# Revit family: HERZ Strömax 4125 AWD
name_source: partatom
category: Rohrzubehör
units: mm (PartAtom-declared; Revit-internal decimal feet)

## family parameters
Arbeitsebenenbasiert = Nein
Beim Laden mit Abzugskörper schneiden = Nein
Bemaßung runder Anschluss = Durchmesser verwenden
Gemeinsam genutzt = Nein
Immer vertikal = Ja
OmniClass-Nummer = 23.65.55.14
OmniClass-Titel = Valves for Liquid Services
Teiletyp = Unterbricht

## types (1)
- HERZ Strömax 4125 AWD
    Application = For shutting off drinking water pipes in buildings.
    Body = DZR brass CC770S
    Hand wheel = plastic, green
    Hersteller = HERZ Armaturen Ges.m.b.H.
    L03 = 15 mm  [stored 0.0492126 ft]
    Max. differential pressure on closed seat = 1000000.0 Pa
    Max. operating pressure = 2000000.0 Pa
    Max. operating pressure (ÖVGW) = 1000000.0 Pa
    Max. operating temperature = 80 °C
    Max. service temperature (ÖVGW) = 65 °C
    Medium = Water
    Note = Pursuant to Article 33 of the REACH Regulation (EC No. 1907/2006), we are obliged to point out that the material lead is listed on the SVHC list and that all brass components manufactured in our products exceed 0.1% (w / w) lead (CAS: 7439-92-1 / EINECS: 231-100-4).
Since lead is a component part of an alloy, actual exposure is not possible and therefore no additional information on safe use is necessary.
    Occasional temperature rises = up to 95°C, if they do not last longer than 1 h
    Plug = DZR brass CW626N
    R03 = 9.5 mm  [stored 0.031168 ft]
    R100 = 1 mm  [stored 0.00328084 ft]
    S03 = 60 mm
    SCTWCODE = 04;00;02
    SCTWSEQ = FW;SBT_TYP_FW="109";2
    SC_NennweiteBerechnet = 0
    SW01 = 60.00°
    Seals = EPDM
    Spindle = forged brass CW617N
    URL = www.herzvalves.com
    Upper part = DZR brass CW626N
    Vorgabe-Ansicht = 0 mm  [stored 0 ft]
    W01 = 45.00°

note: [stored X ft] marks values corroborated as IEEE doubles in the binary element streams (Revit-internal decimal feet)
